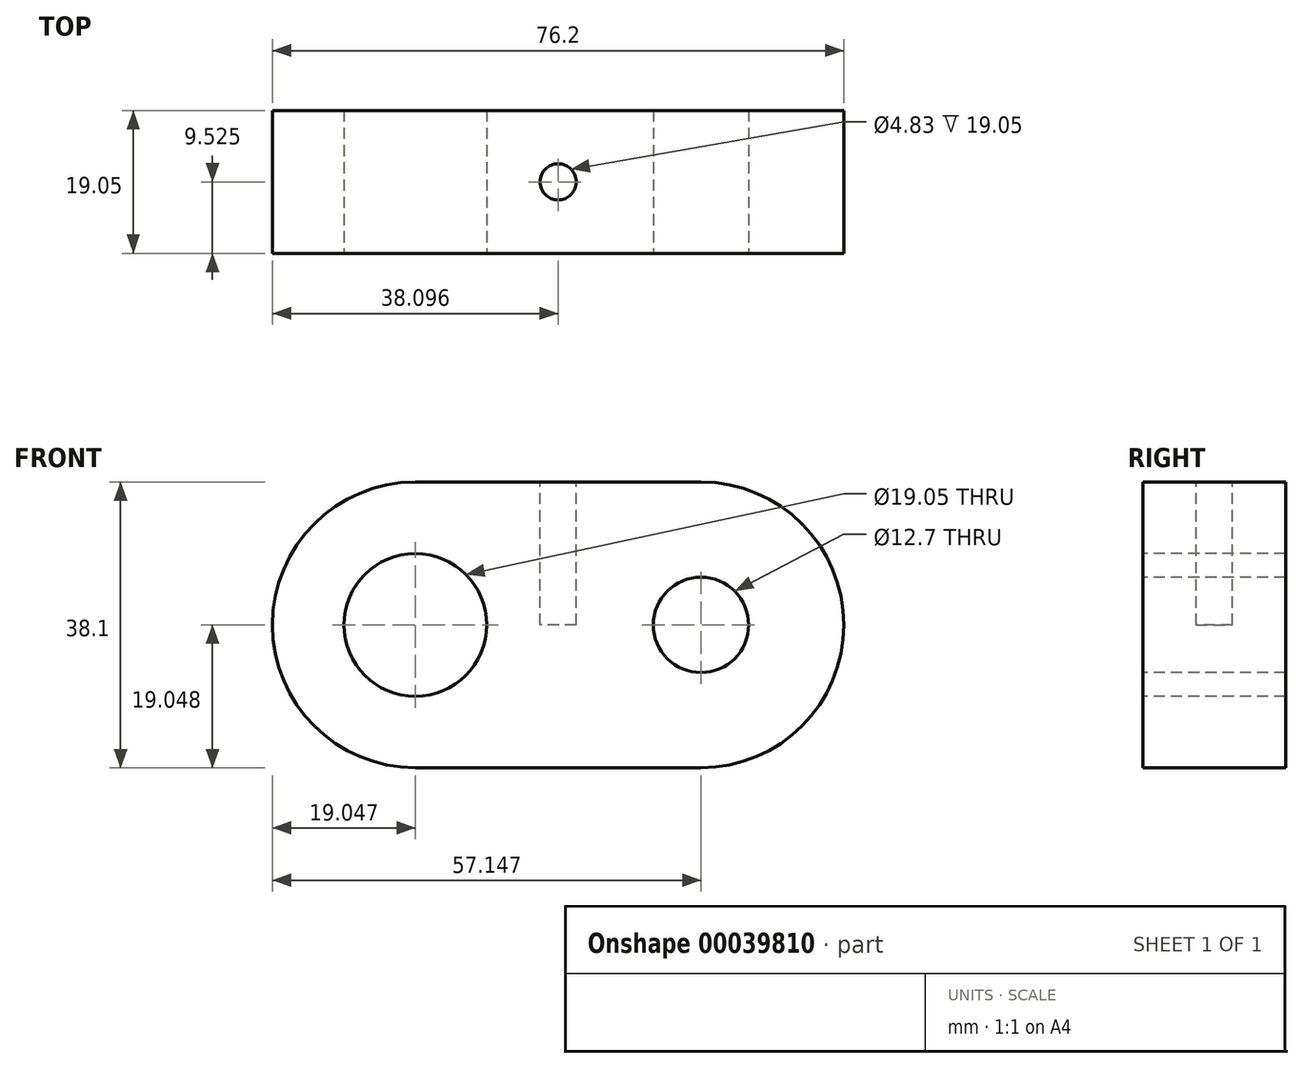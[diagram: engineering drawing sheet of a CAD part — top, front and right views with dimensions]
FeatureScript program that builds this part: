
annotation { "Feature Type Name" : "Feature", "Feature Type Description" : "" }
export const myFeature = defineFeature(function(context is Context, id is Id, definition is map)
    precondition{}
    {
        {
            var Q0;
            Q0=qCreatedBy(makeId("Front.planeOp"),FACE);
            var sketch = newSketch(context, id + "F0", { "sketchPlane" : qUnion([Q0])});
            skLineSegment(sketch, "E0.bottom", {"start": v(-18.45, 0.8) * mm, "end": v(19.65, 0.8) * mm});
            skLineSegment(sketch, "E0.top", {"start": v(-18.45, 38.9) * mm, "end": v(19.65, 38.9) * mm});
            skLineSegment(sketch, "E0.left", {"start": v(-37.5, 19.86) * mm, "end": v(-37.5, 19.86) * mm});
            skLineSegment(sketch, "E0.right", {"start": v(38.7, 19.86) * mm, "end": v(38.7, 19.86) * mm});
            skPoint(sketch, "E1.visualSharp", {"position": v(-37.5, 38.9) * mm});
            skArc(sketch, "E1.filletArc", {"start": v(-18.45, 38.9) * mm, "mid": v(-31.92, 33.33) * mm, "end": v(-37.5, 19.86) * mm});
            skPoint(sketch, "E2.visualSharp", {"position": v(38.7, 38.9) * mm});
            skArc(sketch, "E2.filletArc", {"start": v(38.7, 19.86) * mm, "mid": v(33.12, 33.33) * mm, "end": v(19.65, 38.9) * mm});
            skPoint(sketch, "E3.visualSharp", {"position": v(38.7, 0.8) * mm});
            skArc(sketch, "E3.filletArc", {"start": v(19.65, 0.8) * mm, "mid": v(33.12, 6.39) * mm, "end": v(38.7, 19.86) * mm});
            skPoint(sketch, "E4.visualSharp", {"position": v(-37.5, 0.8) * mm});
            skArc(sketch, "E4.filletArc", {"start": v(-37.5, 19.86) * mm, "mid": v(-31.92, 6.39) * mm, "end": v(-18.45, 0.8) * mm});
            skCircle(sketch, "E5", {"center": v(-18.45, 19.86) * mm, "radius": 9.53 * mm});
            skCircle(sketch, "E6", {"center": v(19.65, 19.86) * mm, "radius": 6.35 * mm});
            skSolve(sketch);
        }
        {
            var Q0;
            Q0=makeQuery(id+"F0.imprint","IMPRINT",FACE,{"disambiguationData":[TD([[makeQuery(id+"F0.imprint","IMPRINT",EDGE,{"derivedFrom":sQuery(id+"F0.wireOp",EDGE,"E0.bottom")}),1.0]])]});
            extrude(context, id + "F1", {"entities" : qUnion([Q0]), "oppositeDirection" : true, "depth" : 19.05 * mm});
        }
        {
            var Q0;
            Q0=makeQuery(id+"F1.opExtrude","SWEPT_FACE",FACE,{"disambiguationData":[OSD([sQuery(id+"F0.wireOp",EDGE,"E0.top")])]});
            var sketch = newSketch(context, id + "F2", { "sketchPlane" : qUnion([Q0])});
            skLineSegment(sketch, "E7", {"start": v(-37.5, 0) * mm, "end": v(-37.5, 19.05) * mm});
            skLineSegment(sketch, "E8", {"start": v(38.7, 19.05) * mm, "end": v(38.7, 0) * mm});
            skCircle(sketch, "E9", {"center": v(0.6, 9.53) * mm, "radius": 2.41 * mm});
            skSolve(sketch);
        }
        {
            var Q0;
            Q0=makeQuery(id+"F2.imprint","IMPRINT",FACE,{"disambiguationData":[TD([[makeQuery(id+"F2.imprint","IMPRINT",EDGE,{"derivedFrom":sQuery(id+"F2.wireOp",EDGE,"E9")}),1.0]])]});
            extrude(context, id + "F3", {"entities" : qUnion([Q0]), "operationType" : NewBodyOperationType.REMOVE, "oppositeDirection" : true, "depth" : 19.05 * mm});
        }
    });
